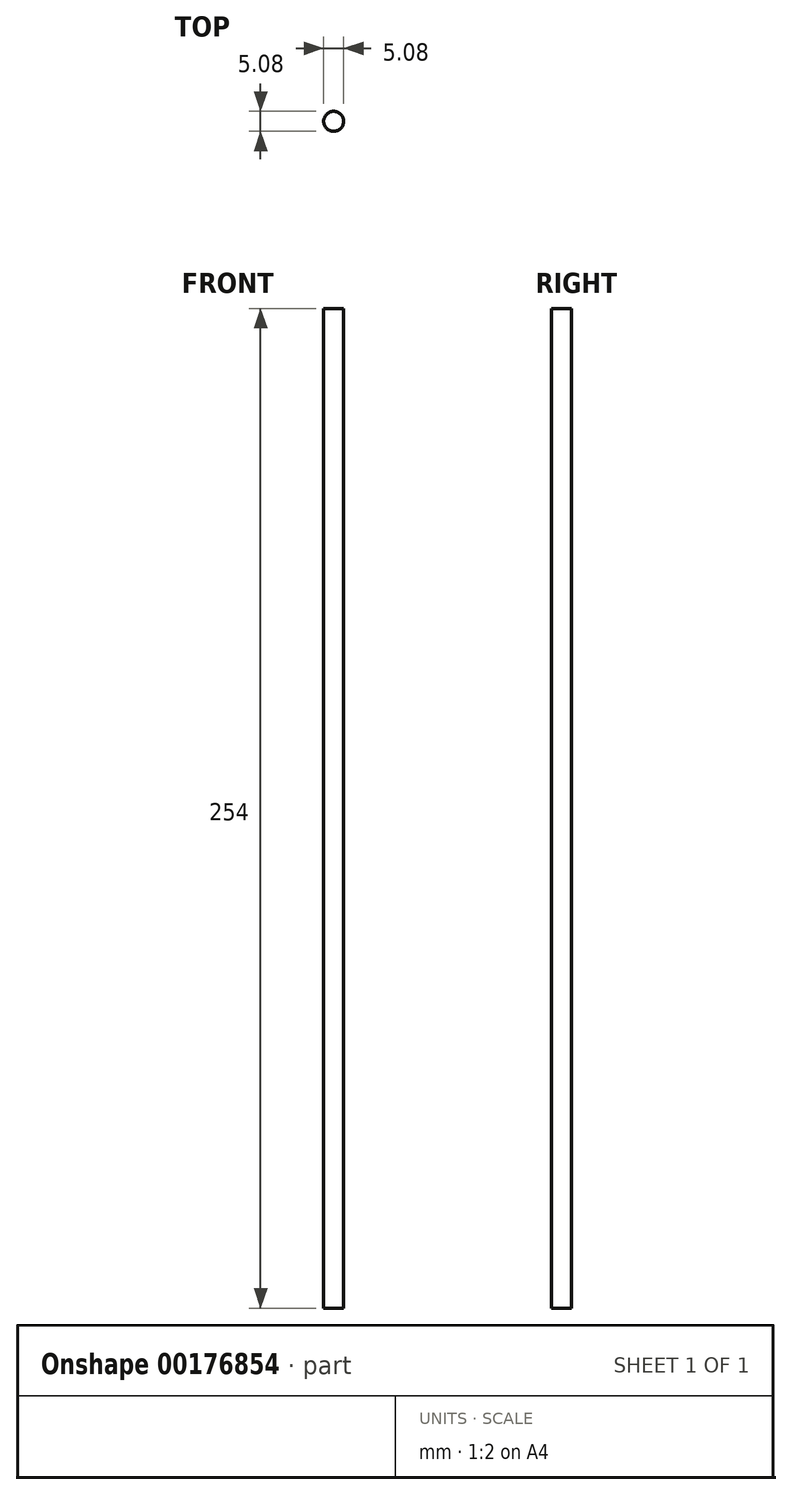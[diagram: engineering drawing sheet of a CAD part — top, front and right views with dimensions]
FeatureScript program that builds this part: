
annotation { "Feature Type Name" : "Feature", "Feature Type Description" : "" }
export const myFeature = defineFeature(function(context is Context, id is Id, definition is map)
    precondition{}
    {
        {
            var Q0;
            Q0=qCreatedBy(makeId("Top.planeOp"),FACE);
            var sketch = newSketch(context, id + "F0", { "sketchPlane" : qUnion([Q0])});
            skCircle(sketch, "E0", {"center": v(0, 0) * mm, "radius": 2.54 * mm});
            skSolve(sketch);
        }
        {
            var Q0;
            Q0 = qSketchRegion(id + "F0", true);
            extrude(context, id + "F1", {"entities" : qUnion([Q0]), "depth" : 254 * mm});
        }
    });
